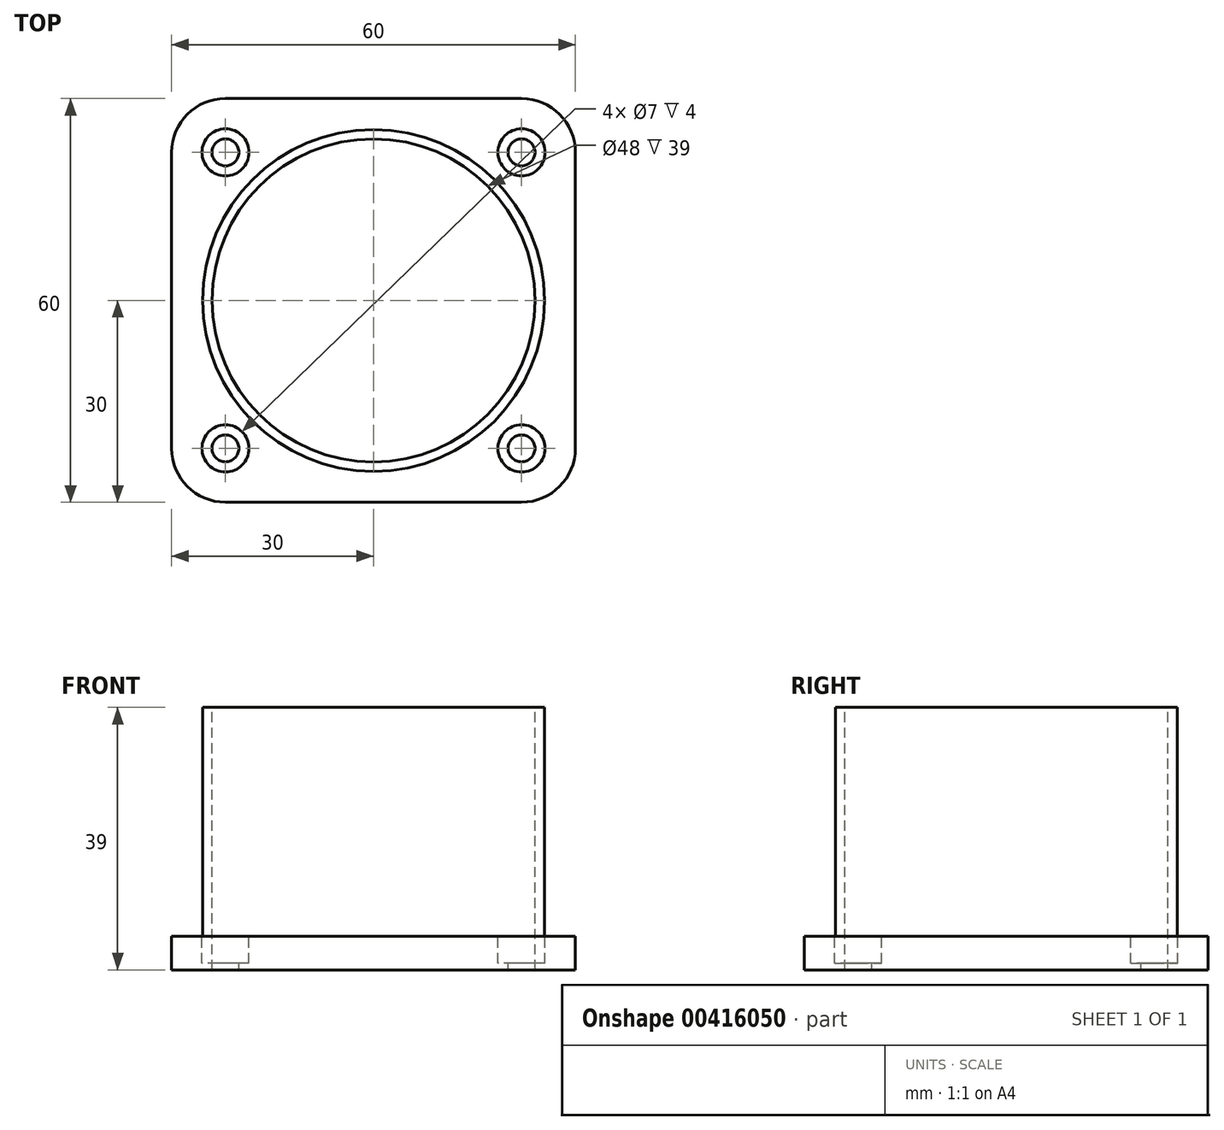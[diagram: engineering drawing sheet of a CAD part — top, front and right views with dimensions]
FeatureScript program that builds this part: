
annotation { "Feature Type Name" : "Feature", "Feature Type Description" : "" }
export const myFeature = defineFeature(function(context is Context, id is Id, definition is map)
    precondition{}
    {
        {
            var Q0;
            Q0=qCreatedBy(makeId("Top.planeOp"),FACE);
            var sketch = newSketch(context, id + "F0", { "sketchPlane" : qUnion([Q0])});
            skLineSegment(sketch, "E0.bottom", {"start": v(-22, 30) * mm, "end": v(22, 30) * mm});
            skLineSegment(sketch, "E0.top", {"start": v(-22, -30) * mm, "end": v(22, -30) * mm});
            skLineSegment(sketch, "E0.left", {"start": v(-30, 22) * mm, "end": v(-30, -22) * mm});
            skLineSegment(sketch, "E0.right", {"start": v(30, 22) * mm, "end": v(30, -22) * mm});
            skArc(sketch, "E1.filletArc", {"start": v(-22, 30) * mm, "mid": v(-27.66, 27.66) * mm, "end": v(-30, 22) * mm});
            skPoint(sketch, "E2.visualSharp", {"position": v(30, 30) * mm});
            skArc(sketch, "E2.filletArc", {"start": v(30, 22) * mm, "mid": v(27.66, 27.66) * mm, "end": v(22, 30) * mm});
            skPoint(sketch, "E3.visualSharp", {"position": v(30, -30) * mm});
            skArc(sketch, "E3.filletArc", {"start": v(22, -30) * mm, "mid": v(27.66, -27.66) * mm, "end": v(30, -22) * mm});
            skPoint(sketch, "E4.visualSharp", {"position": v(-30, -30) * mm});
            skArc(sketch, "E4.filletArc", {"start": v(-30, -22) * mm, "mid": v(-27.66, -27.66) * mm, "end": v(-22, -30) * mm});
            skCircle(sketch, "E5", {"center": v(0, 0) * mm, "radius": 24 * mm});
            skSolve(sketch);
        }
        {
            var Q0;
            Q0=makeQuery(id+"F0.imprint","IMPRINT",FACE,{"disambiguationData":[TD([[makeQuery(id+"F0.imprint","IMPRINT",EDGE,{"derivedFrom":sQuery(id+"F0.wireOp",EDGE,"E0.bottom")}),-1.0]])]});
            extrude(context, id + "F1", {"entities" : qUnion([Q0]), "depth" : -5 * mm});
        }
        {
            var Q0;
            Q0=makeQuery(id+"F0.imprint","IMPRINT",FACE,{"disambiguationData":[TD([[makeQuery(id+"F0.imprint","IMPRINT",EDGE,{"derivedFrom":sQuery(id+"F0.wireOp",EDGE,"E0.bottom")}),-1.0]])]});
            var sketch = newSketch(context, id + "F2", { "sketchPlane" : qUnion([Q0])});
            skCircle(sketch, "E6", {"center": v(0, 0) * mm, "radius": 24 * mm});
            skCircle(sketch, "E7", {"center": v(0, 0) * mm, "radius": 25.4 * mm});
            skSolve(sketch);
        }
        {
            var Q0;
            Q0 = qSketchRegion(id + "F2", true);
            extrude(context, id + "F3", {"entities" : qUnion([Q0]), "operationType" : NewBodyOperationType.ADD, "depth" : 34 * mm});
        }
        {
            var Q0;
            Q0=sQuery(id+"F0.wireOp",VERTEX,"E4.filletArc.center");
            var Q1;
            Q1=sQuery(id+"F0.wireOp",VERTEX,"E3.filletArc.center");
            var Q2;
            Q2=sQuery(id+"F0.wireOp",VERTEX,"E2.filletArc.center");
            var Q3;
            Q3=sQuery(id+"F0.wireOp",VERTEX,"E1.filletArc.center");
            var Q4;
            Q4=makeQuery(id+"F1.opExtrude","SWEPT_BODY",BODY,{"disambiguationData":[OSD([sQuery(id+"F0.wireOp",EDGE,"E0.bottom"),sQuery(id+"F0.wireOp",EDGE,"E0.top"),sQuery(id+"F0.wireOp",EDGE,"E0.left"),sQuery(id+"F0.wireOp",EDGE,"E0.right"),sQuery(id+"F0.wireOp",EDGE,"E1.filletArc"),sQuery(id+"F0.wireOp",EDGE,"E2.filletArc"),sQuery(id+"F0.wireOp",EDGE,"E3.filletArc"),sQuery(id+"F0.wireOp",EDGE,"E4.filletArc"),sQuery(id+"F0.wireOp",EDGE,"E5")])]});
            hole(context, id + "F4", {"style" : HoleStyle.C_BORE, "endStyle" : HoleEndStyle.THROUGH, "holeDiameter" : 4 * mm, "cBoreDiameter" : 7 * mm, "cBoreDepth" : 4 * mm, "tappedDepth" : 12 * mm, "tapClearance" : 3, "locations" : qUnion([Q0, Q1, Q2, Q3]), "scope" : qUnion([Q4])});
        }
    });
